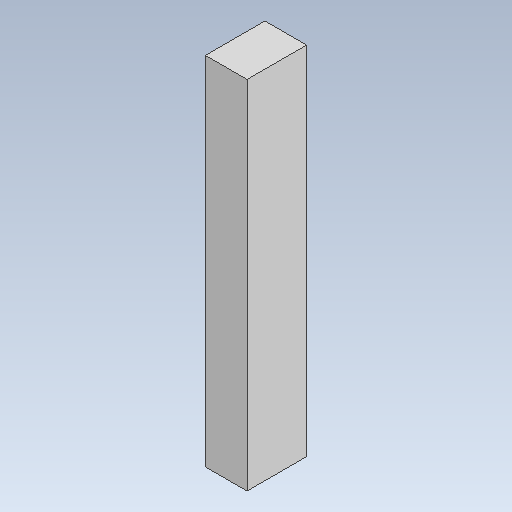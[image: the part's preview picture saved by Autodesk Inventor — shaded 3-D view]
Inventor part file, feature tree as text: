
AUTODESK INVENTOR PART (.ipt)
format: ipt  version: 2021 (Build 250183000, 183)  size: 91,648 bytes
history: native  units: mm
features: extrude x1, sketch x1
ambient origin geometry x8: Origin, YZ Plane, XZ Plane, XY Plane, X Axis, Y Axis, Z Axis, Center Point
bodies: Solid1 (feature_tree)
feature tree (2):
  extrude  "Extrusion1"  Depth=10.0mm
  sketch  "Sketch2"  dims[d2=7.0mm d3=10.0mm d4=59.873mm d5=0.0mm]
